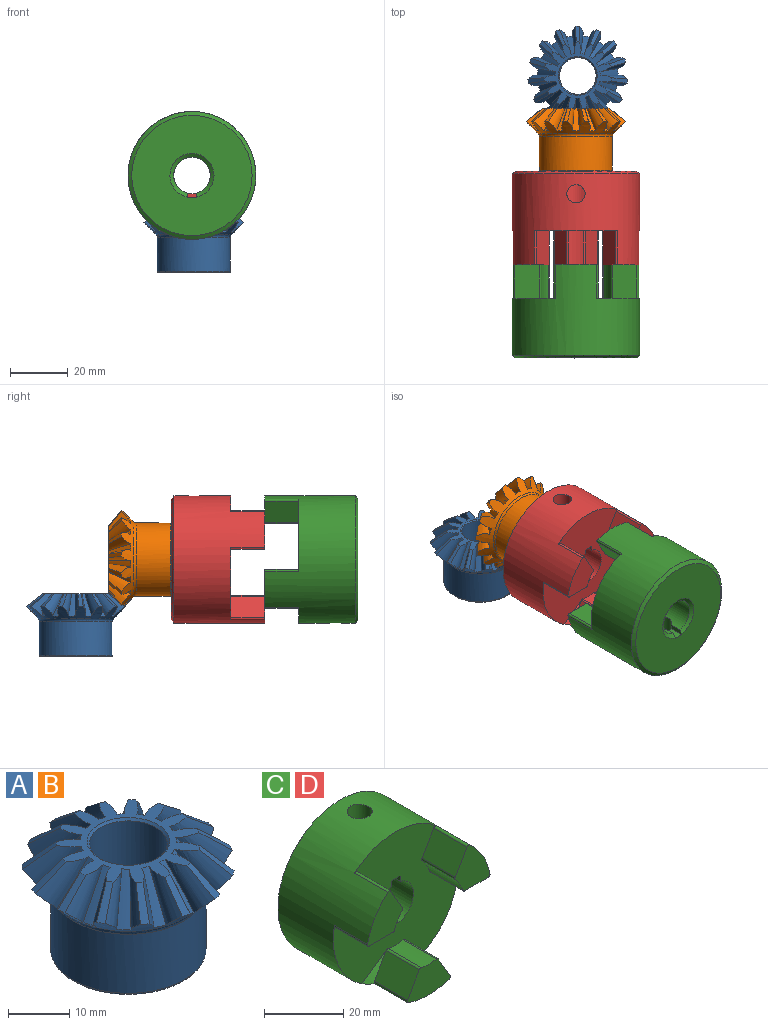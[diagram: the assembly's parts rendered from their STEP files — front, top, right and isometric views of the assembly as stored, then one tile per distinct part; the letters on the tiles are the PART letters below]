
ASSEMBLY  parts=4 mates=2
PART A: 69 faces, bbox 35.8x35.6x24.1 mm
  f0: cone r=6.75mm half-angle=45deg, axis (0,0,1), area 23.1mm2, adj f15,f17
  f1: cone r=17.37mm half-angle=51.4deg, axis (0,0,-1), area 9.5mm2, adj f15,f18,f19,f64
  f2: cone r=17.37mm half-angle=51.4deg, axis (0,0,-1), area 9.5mm2, adj f15,f21,f22,f64
  f3: cone r=17.37mm half-angle=51.4deg, axis (0,0,-1), area 9.5mm2, adj f15,f24,f25,f64
  f4: cone r=17.37mm half-angle=51.4deg, axis (0,0,-1), area 9.5mm2, adj f15,f27,f28,f64
  f5: cone r=17.37mm half-angle=51.4deg, axis (0,0,-1), area 9.5mm2, adj f15,f30,f31,f64
  f6: cone r=17.37mm half-angle=51.4deg, axis (0,0,-1), area 9.5mm2, adj f15,f33,f34,f64
  f7: cone r=17.37mm half-angle=51.4deg, axis (0,0,-1), area 9.5mm2, adj f15,f36,f37,f64
  f8: cone r=17.37mm half-angle=51.4deg, axis (0,0,-1), area 9.5mm2, adj f15,f39,f40,f64
  f9: cone r=17.37mm half-angle=51.4deg, axis (0,0,-1), area 9.5mm2, adj f15,f42,f43,f64
  f10: cone r=17.37mm half-angle=51.4deg, axis (0,0,-1), area 9.5mm2, adj f15,f45,f46,f64
  f11: cone r=17.37mm half-angle=51.4deg, axis (0,0,-1), area 9.5mm2, adj f15,f48,f49,f64
  f12: cone r=17.37mm half-angle=51.4deg, axis (0,0,-1), area 9.5mm2, adj f15,f51,f52,f64
  f13: cone r=17.37mm half-angle=51.4deg, axis (0,0,-1), area 9.5mm2, adj f15,f54,f55,f64
  f14: cone r=17.37mm half-angle=51.4deg, axis (0,0,-1), area 9.5mm2, adj f15,f57,f58,f64
  f15: plane 23.8x23.68mm, normal (0,0,1), area 164.6mm2, adj f0,f1,f2,f3,f4,f5,f6,f7
  f16: cone r=17.37mm half-angle=51.4deg, axis (0,0,-1), area 9.5mm2, adj f15,f60,f61,f64
  f17: cylinder r=6.36mm len=21.03mm, axis (0,0,-1), area 839.7mm2, adj f0,f63
  f18: bspline ~10.01x9.39mm, area 33.4mm2, adj f1,f15,f62,f64
  f19: bspline ~9.58x8.74mm, area 33.3mm2, adj f1,f15,f20,f64
  f20: bspline ~7.77x6.44mm, area 18.2mm2, adj f15,f19,f21,f64
  f21: bspline ~10.15x10.01mm, area 33.4mm2, adj f2,f15,f20,f64
  f22: bspline ~10.15x10.01mm, area 33.3mm2, adj f2,f15,f23,f64
  f23: bspline ~7.77x6.44mm, area 18.2mm2, adj f15,f22,f24,f64
  f24: bspline ~9.58x8.74mm, area 33.4mm2, adj f3,f15,f23,f64
  f25: bspline ~10.01x9.39mm, area 33.3mm2, adj f3,f15,f26,f64
  f26: bspline ~7.77x6.09mm, area 18.2mm2, adj f15,f25,f27,f64
  f27: bspline ~10.01x7.73mm, area 33.4mm2, adj f4,f15,f26,f64
  f28: bspline ~9.58x7.03mm, area 33.3mm2, adj f4,f15,f29,f64
  f29: bspline ~7.77x6.28mm, area 18.2mm2, adj f15,f28,f30,f64
  f30: bspline ~10.01x9.74mm, area 33.4mm2, adj f5,f15,f29,f64
  f31: bspline ~9.58x9.13mm, area 33.3mm2, adj f5,f15,f32,f64
  f32: bspline ~8.19x6.68mm, area 18.2mm2, adj f15,f31,f33,f64
  f33: bspline ~10.07x10.01mm, area 33.4mm2, adj f6,f15,f32,f64
  f34: bspline ~9.64x9.58mm, area 33.3mm2, adj f6,f15,f35,f64
  f35: bspline ~7.77x6.46mm, area 18.2mm2, adj f15,f34,f36,f64
  f36: bspline ~9.58x8.26mm, area 33.4mm2, adj f7,f15,f35,f64
  f37: bspline ~9.58x8.49mm, area 33.3mm2, adj f7,f15,f38,f64
  f38: bspline ~7.77x5.83mm, area 18.2mm2, adj f15,f37,f39,f64
  f39: bspline ~10.01x8.38mm, area 33.4mm2, adj f8,f15,f38,f64
  f40: bspline ~9.58x7.69mm, area 33.3mm2, adj f8,f15,f41,f64
  f41: bspline ~8.19x6.71mm, area 18.2mm2, adj f15,f40,f42,f64
  f42: bspline ~10.01x9.99mm, area 33.4mm2, adj f9,f15,f41,f64
  f43: bspline ~10.01x9.87mm, area 33.3mm2, adj f9,f15,f44,f64
  f44: bspline ~8.19x6.56mm, area 18.2mm2, adj f15,f43,f45,f64
  f45: bspline ~10.01x9.87mm, area 33.4mm2, adj f10,f15,f44,f64
  f46: bspline ~10.01x9.99mm, area 33.3mm2, adj f10,f15,f47,f64
  f47: bspline ~8.19x6.71mm, area 18.2mm2, adj f15,f46,f48,f64
  f48: bspline ~9.58x7.69mm, area 33.4mm2, adj f11,f15,f47,f64
  f49: bspline ~10.01x8.38mm, area 33.3mm2, adj f11,f15,f50,f64
  f50: bspline ~7.77x5.83mm, area 18.2mm2, adj f15,f49,f51,f64
  f51: bspline ~9.58x8.49mm, area 33.4mm2, adj f12,f15,f50,f64
  f52: bspline ~9.58x8.26mm, area 33.3mm2, adj f12,f15,f53,f64
  f53: bspline ~7.77x6.46mm, area 18.2mm2, adj f15,f52,f54,f64
  f54: bspline ~9.64x9.58mm, area 33.4mm2, adj f13,f15,f53,f64
  f55: bspline ~10.07x10.01mm, area 33.3mm2, adj f13,f15,f56,f64
  f56: bspline ~8.19x6.68mm, area 18.2mm2, adj f15,f55,f57,f64
  f57: bspline ~9.58x9.13mm, area 33.4mm2, adj f14,f15,f56,f64
  f58: bspline ~10.01x9.74mm, area 33.3mm2, adj f14,f15,f59,f64
  f59: bspline ~7.77x6.28mm, area 18.2mm2, adj f15,f58,f60,f64
  f60: bspline ~9.58x7.03mm, area 33.4mm2, adj f15,f16,f59,f64
  f61: bspline ~10.01x7.73mm, area 33.3mm2, adj f15,f16,f62,f64
  f62: bspline ~7.77x6.09mm, area 18.2mm2, adj f15,f18,f61,f64
  f63: cone r=6.75mm half-angle=45deg, axis (0,0,-1), area 23.1mm2, adj f17,f65
  f64: cone r=17.37mm half-angle=45deg, axis (0,0,1), area 305.1mm2, adj f1,f2,f3,f4,f5,f6,f7,f8
  f65: plane 24.61x24.61mm, normal (0,0,-1), area 331.1mm2, adj f63,f67
  f66: torus R=13.89mm, axis (0,0,1), area 75.5mm2, adj f64,f68
  f67: torus R=12.3mm, axis (0,0,-1), area 49.2mm2, adj f65,f68
  f68: cylinder r=12.7mm len=25.4mm, axis (0,0,-1), area 942.3mm2, adj f66,f67
PART B: same geometry as A
PART C: 37 faces, bbox 44.5x32.5x44.5 mm
  f0: cylinder r=22.23mm len=44.45mm, axis (0,-1,0), area 3249.2mm2, adj f8,f9,f15,f16,f17,f23,f25,f29
  f1: cylinder r=6.35mm len=19.75mm, axis (0,-1,0), area 711.3mm2, adj f2,f3,f6,f7,f25,f34,f36
  f2: plane 5.15x1.62mm, normal (1,0,0), area 7.5mm2, adj f1,f4,f24,f34,f36
  f3: plane 10.01x1.59mm, normal (1,0,0), area 15.9mm2, adj f1,f5,f25,f36
  f4: plane 5.12x3.18mm, normal (0,0,-1), area 15.4mm2, adj f2,f7,f24,f36
  f5: plane 10.01x3.18mm, normal (0,0,-1), area 30.9mm2, adj f3,f6,f25,f36
  f6: plane 10.01x1.59mm, normal (-1,0,0), area 15.9mm2, adj f1,f5,f25,f36
  f7: plane 5.15x1.62mm, normal (-1,0,0), area 7.5mm2, adj f1,f4,f24,f34,f36
  f8: cylinder r=0.63mm len=11.81mm, axis (0,-1,0), area 13.1mm2, adj f0,f13,f15,f25
  f9: cylinder r=0.63mm len=11.81mm, axis (0,-1,0), area 13.1mm2, adj f0,f14,f15,f25
  f10: cylinder r=0.63mm len=11.81mm, axis (0,1,0), area 9.4mm2, adj f12,f14,f15,f25
  f11: cylinder r=0.63mm len=11.81mm, axis (0,1,0), area 9.4mm2, adj f12,f13,f15,f25
  f12: cylinder r=12.8mm len=11.81mm, axis (0,1,0), area 64.3mm2, adj f10,f11,f15,f25
  f13: plane 11.81x7.29mm, normal (0.87,0,0.5), area 99.4mm2, adj f8,f11,f15,f25
  f14: plane 11.81x8.41mm, normal (0,0,-1), area 99.4mm2, adj f9,f10,f15,f25
  f15: plane 13.46x12.51mm, normal (0,-1,0), area 106.4mm2, adj f0,f8,f9,f10,f11,f12,f13,f14
  f16: cylinder r=0.63mm len=11.81mm, axis (0,-1,0), area 13.1mm2, adj f0,f21,f23,f25
  f17: cylinder r=0.63mm len=11.81mm, axis (0,-1,0), area 13.1mm2, adj f0,f22,f23,f25
  f18: cylinder r=0.63mm len=11.81mm, axis (0,1,0), area 9.4mm2, adj f20,f22,f23,f25
  f19: cylinder r=0.63mm len=11.81mm, axis (0,1,0), area 9.4mm2, adj f20,f21,f23,f25
  f20: cylinder r=12.8mm len=11.81mm, axis (0,1,0), area 64.3mm2, adj f18,f19,f23,f25
  f21: plane 11.81x8.41mm, normal (0,0,-1), area 99.4mm2, adj f16,f19,f23,f25
  f22: plane 11.81x7.29mm, normal (-0.87,0,0.5), area 99.4mm2, adj f17,f18,f23,f25
  f23: plane 13.46x12.51mm, normal (0,-1,0), area 106.4mm2, adj f0,f16,f17,f18,f19,f20,f21,f22
  f24: plane 41.81x41.81mm, normal (0,1,0), area 1188.1mm2, adj f2,f4,f7,f34,f35
  f25: plane 44.45x43.24mm, normal (0,-1,0), area 1101.2mm2, adj f0,f1,f3,f5,f6,f8,f9,f10
  f26: cylinder r=12.8mm len=11.81mm, axis (0,1,0), area 64.3mm2, adj f25,f29,f32,f33
  f27: plane 11.81x7.29mm, normal (-0.87,0,0.5), area 99.4mm2, adj f25,f29,f30,f33
  f28: plane 11.81x7.29mm, normal (0.87,0,0.5), area 99.4mm2, adj f25,f29,f31,f32
  f29: plane 15.34x9.73mm, normal (0,-1,0), area 106.4mm2, adj f0,f26,f27,f28,f30,f31,f32,f33
  f30: cylinder r=0.63mm len=11.81mm, axis (0,-1,0), area 13.1mm2, adj f0,f25,f27,f29
  f31: cylinder r=0.63mm len=11.81mm, axis (0,-1,0), area 13.1mm2, adj f0,f25,f28,f29
  f32: cylinder r=0.63mm len=11.81mm, axis (0,1,0), area 9.4mm2, adj f25,f26,f28,f29
  f33: cylinder r=0.63mm len=11.81mm, axis (0,1,0), area 9.4mm2, adj f25,f26,f27,f29
  f34: cone r=7.67mm half-angle=56deg, axis (0,1,0), area 64.9mm2, adj f1,f2,f7,f24
  f35: cone r=22.23mm half-angle=56deg, axis (0,-1,0), area 215.4mm2, adj f0,f24
  f36: cylinder r=3.17mm len=16.73mm, axis (0,0,-1), area 315.3mm2, adj f0,f1,f2,f3,f4,f5,f6,f7
PART D: same geometry as C
PLACE A t=(56.3,124.46,-30.96)mm
PLACE B rot(axis=(-1,0,0),90deg) t=(55.66,95.5,-1.93)mm
PLACE C rot(axis=(1,0,0),180deg) t=(55.66,53.14,-1.68)mm
PLACE D t=(55.66,64.06,-1.68)mm
MATE cylindrical C.f0 <-> D.f0  axis (0,1,0) through (55.66,42.82,-1.68)mm
MATE planar B.f17 <-> D.f0  axis (0,-1,0) through (55.66,91.05,-1.69)mm
